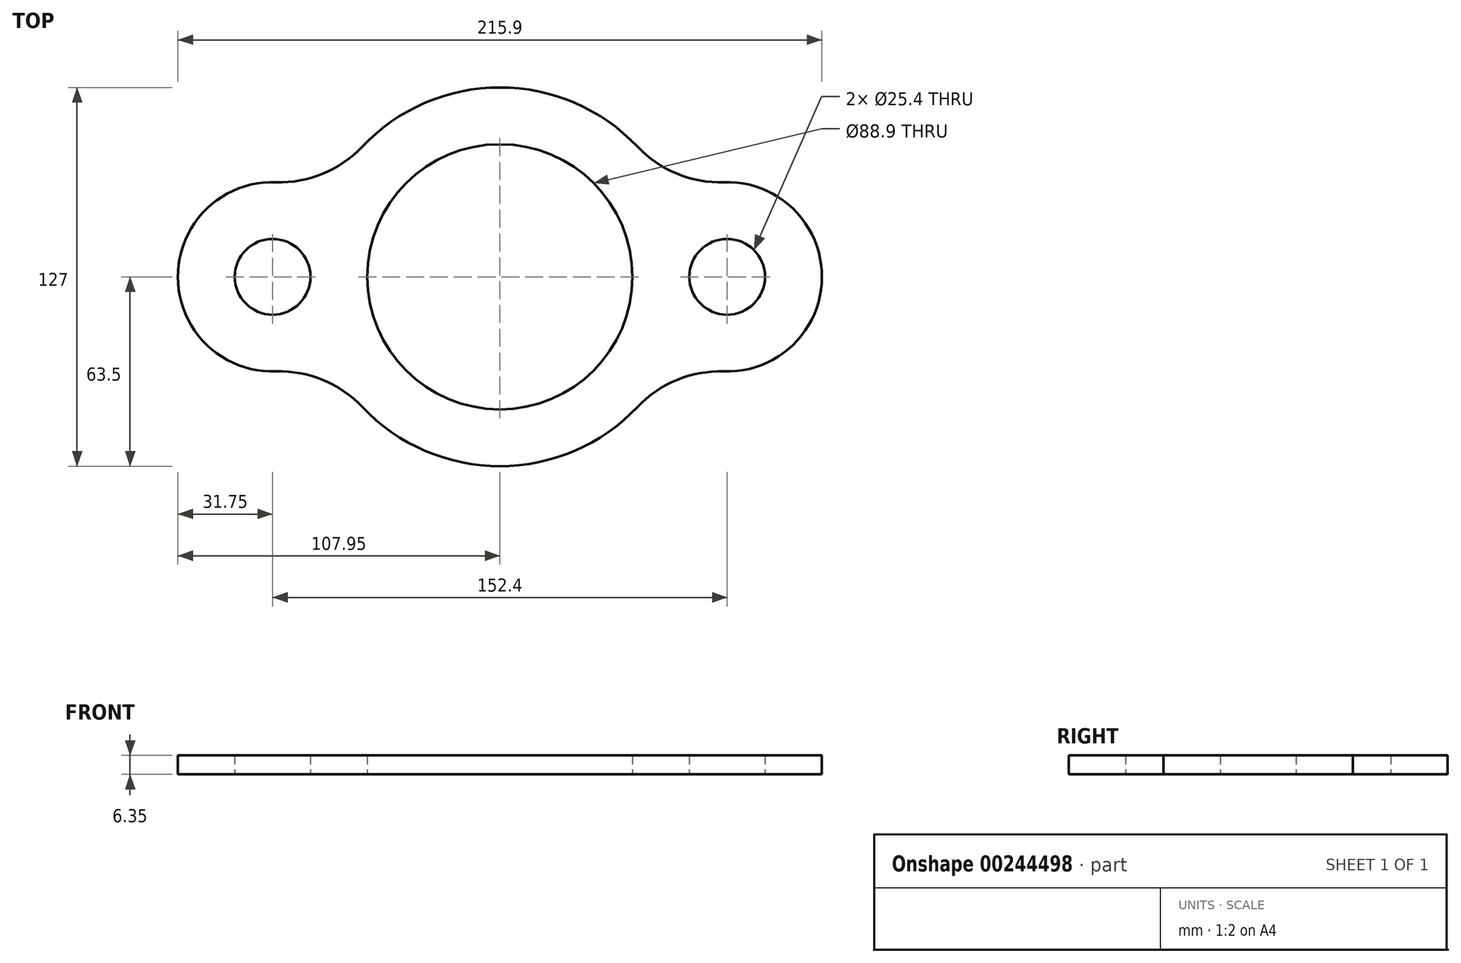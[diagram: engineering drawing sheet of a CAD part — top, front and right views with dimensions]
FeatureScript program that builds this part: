
annotation { "Feature Type Name" : "Feature", "Feature Type Description" : "" }
export const myFeature = defineFeature(function(context is Context, id is Id, definition is map)
    precondition{}
    {
        {
            var Q0;
            Q0=qCreatedBy(makeId("Top.planeOp"),FACE);
            var sketch = newSketch(context, id + "F0", { "sketchPlane" : qUnion([Q0])});
            skCircle(sketch, "E0", {"center": v(0, 0) * mm, "radius": 44.45 * mm});
            skArc(sketch, "E1.0", {"start": v(-46.14, -43.63) * mm, "mid": v(0, -63.5) * mm, "end": v(46.14, -43.63) * mm});
            skCircle(sketch, "E2", {"center": v(-76.2, 0) * mm, "radius": 12.7 * mm});
            skArc(sketch, "E3.0", {"start": v(-75.12, 31.73) * mm, "mid": v(-107.95, 0) * mm, "end": v(-75.12, -31.73) * mm});
            skCircle(sketch, "E4", {"center": v(76.2, 0) * mm, "radius": 12.7 * mm});
            skArc(sketch, "E5.0", {"start": v(75.12, -31.73) * mm, "mid": v(107.95, 0) * mm, "end": v(75.12, 31.73) * mm});
            skArc(sketch, "E6.trimOffspring", {"start": v(46.14, 43.63) * mm, "mid": v(0, 63.5) * mm, "end": v(-46.14, 43.63) * mm});
            skPoint(sketch, "E7.visualSharp", {"position": v(-57.94, 25.98) * mm});
            skArc(sketch, "E7.filletArc", {"start": v(-75.12, 31.73) * mm, "mid": v(-59.35, 34.56) * mm, "end": v(-46.14, 43.63) * mm});
            skPoint(sketch, "E8.visualSharp", {"position": v(57.94, 25.98) * mm});
            skArc(sketch, "E8.filletArc", {"start": v(46.14, 43.63) * mm, "mid": v(59.35, 34.56) * mm, "end": v(75.12, 31.73) * mm});
            skPoint(sketch, "E9.visualSharp", {"position": v(57.94, -25.98) * mm});
            skArc(sketch, "E9.filletArc", {"start": v(75.12, -31.73) * mm, "mid": v(59.35, -34.56) * mm, "end": v(46.14, -43.63) * mm});
            skPoint(sketch, "E10.visualSharp", {"position": v(-57.94, -25.98) * mm});
            skArc(sketch, "E10.filletArc", {"start": v(-46.14, -43.63) * mm, "mid": v(-59.35, -34.56) * mm, "end": v(-75.12, -31.73) * mm});
            skLineSegment(sketch, "E11", {"start": v(-76.2, 0) * mm, "end": v(76.2, 0) * mm, "construction": true});
            skSolve(sketch);
        }
        {
            var Q0;
            Q0 = qSketchRegion(id + "F0", true);
            extrude(context, id + "F1", {"entities" : qUnion([Q0]), "depth" : 6.35 * mm});
        }
    });
